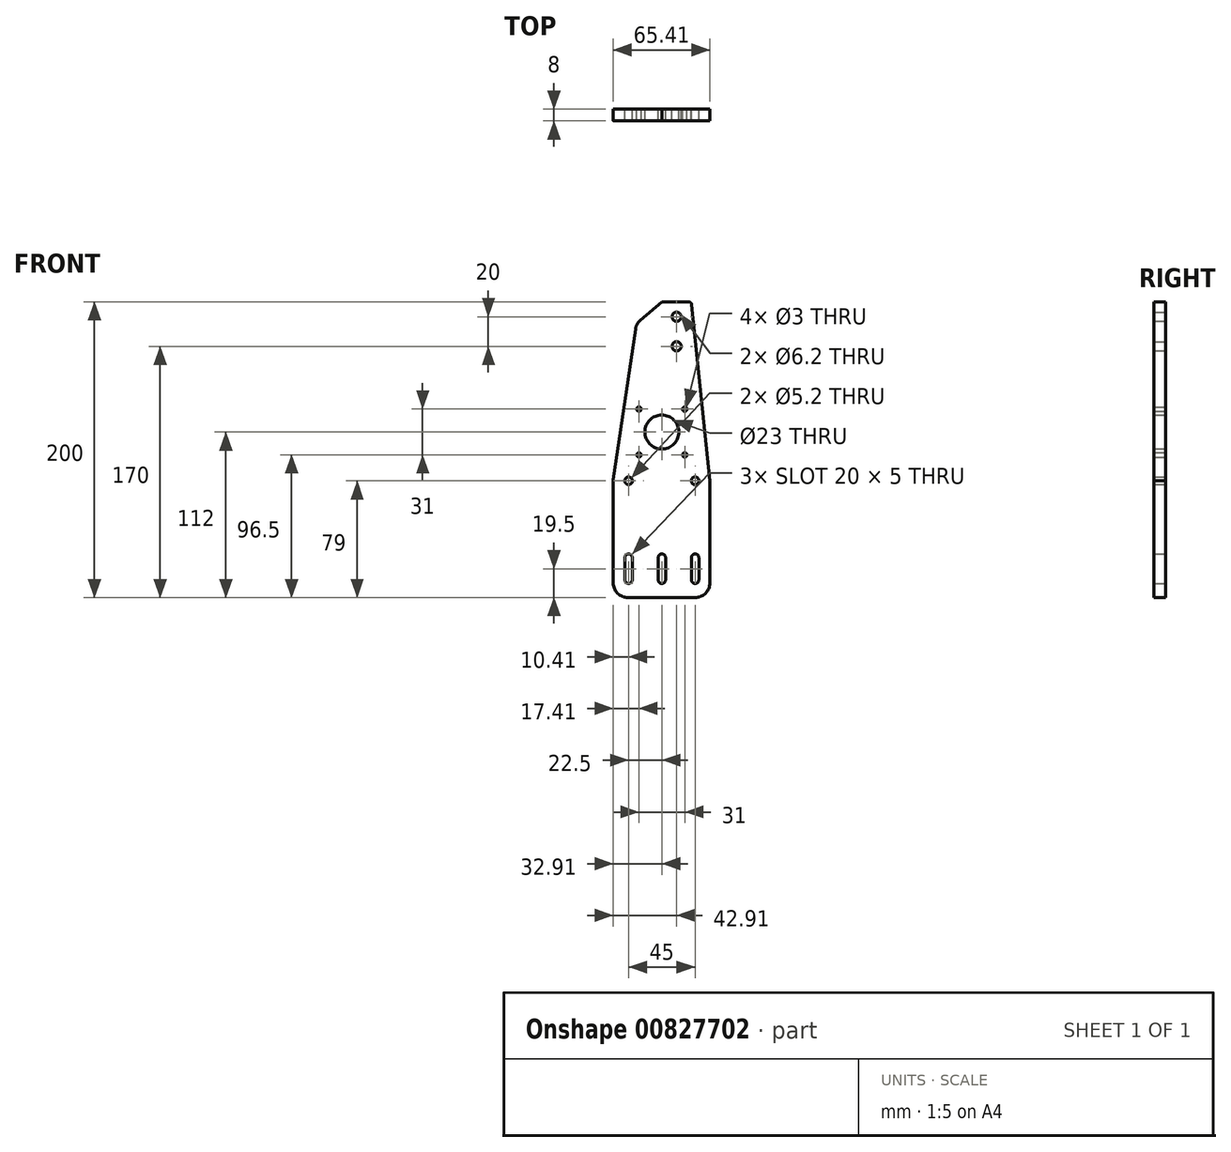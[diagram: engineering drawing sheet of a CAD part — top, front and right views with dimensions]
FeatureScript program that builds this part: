
annotation { "Feature Type Name" : "Feature", "Feature Type Description" : "" }
export const myFeature = defineFeature(function(context is Context, id is Id, definition is map)
    precondition{}
    {
        {
            var Q0;
            Q0=qCreatedBy(makeId("Front.planeOp"),FACE);
            var sketch = newSketch(context, id + "F0", { "sketchPlane" : qUnion([Q0])});
            skPoint(sketch, "E0.middle", {"position": v(0, 0) * mm});
            skCircle(sketch, "E1", {"center": v(10, 90) * mm, "radius": 3.1 * mm});
            skCircle(sketch, "E2", {"center": v(10, 70) * mm, "radius": 3.1 * mm});
            skCircle(sketch, "E3", {"center": v(0, 12) * mm, "radius": 11.5 * mm});
            skCircle(sketch, "E4", {"center": v(-15.5, 27.5) * mm, "radius": 1.5 * mm});
            skCircle(sketch, "E5", {"center": v(15.5, 27.5) * mm, "radius": 1.5 * mm});
            skCircle(sketch, "E6", {"center": v(15.5, -3.5) * mm, "radius": 1.5 * mm});
            skCircle(sketch, "E7", {"center": v(-15.5, -3.5) * mm, "radius": 1.5 * mm});
            skLineSegment(sketch, "E8", {"start": v(-2.5, -76) * mm, "end": v(-2.5, -88) * mm});
            skLineSegment(sketch, "E9", {"start": v(2.5, -80) * mm, "end": v(2.5, -80) * mm});
            skLineSegment(sketch, "E10", {"start": v(2.5, -76) * mm, "end": v(2.5, -88) * mm});
            skArc(sketch, "E11", {"start": v(-2.5, -88) * mm, "mid": v(0, -90.5) * mm, "end": v(2.5, -88) * mm});
            skCircle(sketch, "E12", {"center": v(22.5, -21) * mm, "radius": 2.6 * mm});
            skCircle(sketch, "E13", {"center": v(-22.5, -21) * mm, "radius": 2.6 * mm});
            skLineSegment(sketch, "E14", {"start": v(-25, -73) * mm, "end": v(-25, -88) * mm});
            skLineSegment(sketch, "E15", {"start": v(-15.59, -74.5) * mm, "end": v(-15.59, -74.5) * mm});
            skLineSegment(sketch, "E16", {"start": v(-20, -73) * mm, "end": v(-20, -88) * mm});
            skArc(sketch, "E17", {"start": v(-20, -73) * mm, "mid": v(-22.5, -70.5) * mm, "end": v(-25, -73) * mm});
            skArc(sketch, "E18", {"start": v(-25, -88) * mm, "mid": v(-22.5, -90.5) * mm, "end": v(-20, -88) * mm});
            skLineSegment(sketch, "E19", {"start": v(20, -76) * mm, "end": v(20, -88) * mm});
            skLineSegment(sketch, "E20", {"start": v(24.48, -83.52) * mm, "end": v(24.48, -83.52) * mm});
            skLineSegment(sketch, "E21", {"start": v(25, -76) * mm, "end": v(25, -88) * mm});
            skArc(sketch, "E22", {"start": v(20, -88) * mm, "mid": v(22.5, -90.5) * mm, "end": v(25, -88) * mm});
            skLineSegment(sketch, "E23", {"start": v(0, 12) * mm, "end": v(0, 112.86) * mm, "construction": true});
            skLineSegment(sketch, "E24.bottom", {"start": v(18.2, 100) * mm, "end": v(0, 100) * mm});
            skLineSegment(sketch, "E24.right", {"start": v(0, 100) * mm, "end": v(0, 80) * mm});
            skLineSegment(sketch, "E25.right", {"start": v(0, 60) * mm, "end": v(0, 80) * mm});
            skLineSegment(sketch, "E26", {"start": v(0, 100) * mm, "end": v(-14.45, 87.69) * mm});
            skLineSegment(sketch, "E27", {"start": v(-32.9, -90) * mm, "end": v(-32.9, -21.73) * mm});
            skLineSegment(sketch, "E28", {"start": v(-32.8, -20.28) * mm, "end": v(-17.86, 81.53) * mm});
            skPoint(sketch, "E29.visualSharp", {"position": v(-17.31, 85.25) * mm});
            skArc(sketch, "E29.filletArc", {"start": v(-14.45, 87.69) * mm, "mid": v(-16.71, 84.92) * mm, "end": v(-17.86, 81.53) * mm});
            skPoint(sketch, "E30.visualSharp", {"position": v(-32.9, -21) * mm});
            skArc(sketch, "E30.filletArc", {"start": v(-32.8, -20.28) * mm, "mid": v(-32.88, -21) * mm, "end": v(-32.9, -21.73) * mm});
            skPoint(sketch, "E31.visualSharp", {"position": v(-32.9, -100) * mm});
            skArc(sketch, "E31.filletArc", {"start": v(-32.9, -90) * mm, "mid": v(-29.98, -97.07) * mm, "end": v(-22.9, -100) * mm});
            skLineSegment(sketch, "E32", {"start": v(0, -92) * mm, "end": v(0, -100) * mm, "construction": true});
            skLineSegment(sketch, "E33", {"start": v(0, -100) * mm, "end": v(22.5, -100) * mm});
            skLineSegment(sketch, "E34", {"start": v(0, -100) * mm, "end": v(-22.9, -100) * mm});
            skLineSegment(sketch, "E35", {"start": v(22.5, -100) * mm, "end": v(22.5, -100) * mm});
            skLineSegment(sketch, "E36", {"start": v(32.5, -90) * mm, "end": v(32.5, -21) * mm});
            skLineSegment(sketch, "E37", {"start": v(32.5, -21) * mm, "end": v(20.19, 98.2) * mm});
            skPoint(sketch, "E38.visualSharp", {"position": v(32.5, -100) * mm});
            skArc(sketch, "E38.filletArc", {"start": v(22.5, -100) * mm, "mid": v(29.57, -97.07) * mm, "end": v(32.5, -90) * mm});
            skPoint(sketch, "E39.visualSharp", {"position": v(20, 100) * mm});
            skArc(sketch, "E39.filletArc", {"start": v(20.19, 98.2) * mm, "mid": v(19.54, 99.49) * mm, "end": v(18.2, 100) * mm});
            skLineSegment(sketch, "E40", {"start": v(-2.5, -73) * mm, "end": v(-2.5, -88) * mm});
            skLineSegment(sketch, "E41", {"start": v(2.5, -73) * mm, "end": v(2.5, -88) * mm});
            skArc(sketch, "E42", {"start": v(2.5, -73) * mm, "mid": v(0, -70.5) * mm, "end": v(-2.5, -73) * mm});
            skLineSegment(sketch, "E43", {"start": v(20, -73) * mm, "end": v(20, -88) * mm});
            skLineSegment(sketch, "E44", {"start": v(25, -73) * mm, "end": v(25, -88) * mm});
            skArc(sketch, "E45", {"start": v(25, -73) * mm, "mid": v(22.5, -70.5) * mm, "end": v(20, -73) * mm});
            skSolve(sketch);
        }
        {
            assignVariable(context, id + "F1", {"name" : "Plexiglas", "anyValue" : 8});
        }
        {
            var Q0;
            Q0=makeQuery(id+"F0.imprint","IMPRINT",FACE,{"disambiguationData":[TD([[makeQuery(id+"F0.imprint","IMPRINT",EDGE,{"derivedFrom":sQuery(id+"F0.wireOp",EDGE,"E1")}),-1.0]])]});
            extrude(context, id + "F2", {"entities" : qUnion([Q0]), "flatOperationType" : FlatOperationType.REMOVE, "depth" : (getVariable(context, 'Plexiglas')) * mm, "offsetDistance" : 25 * mm, "domain" : OperationDomain.MODEL});
        }
    });
